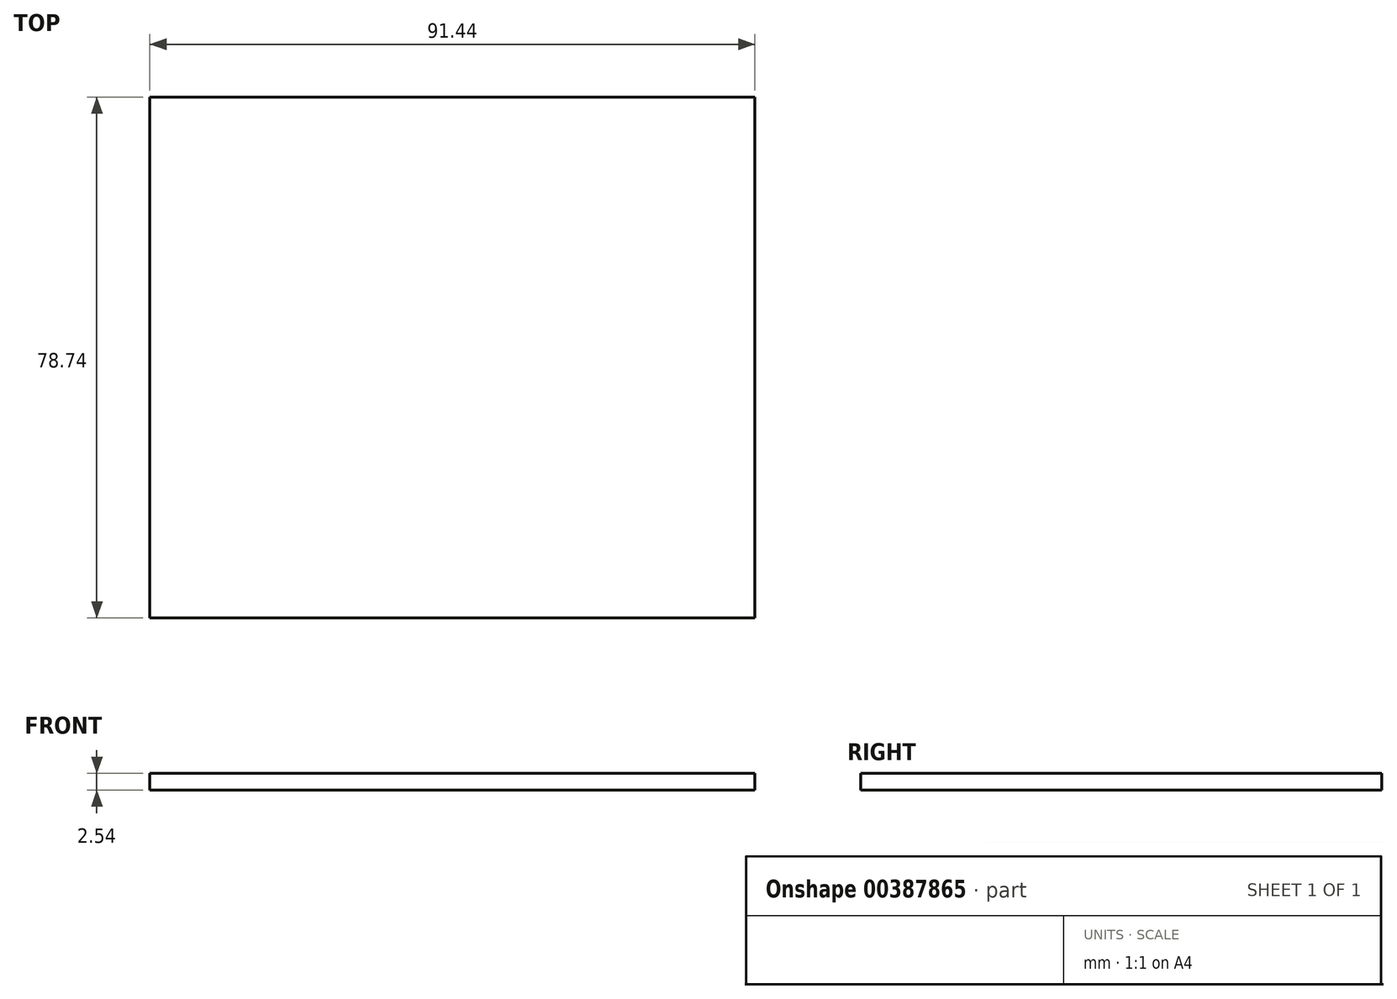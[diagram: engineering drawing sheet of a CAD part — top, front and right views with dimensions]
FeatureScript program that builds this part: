
annotation { "Feature Type Name" : "Feature", "Feature Type Description" : "" }
export const myFeature = defineFeature(function(context is Context, id is Id, definition is map)
    precondition{}
    {
        {
            var Q0;
            Q0=qCreatedBy(makeId("Top.planeOp"),FACE);
            var sketch = newSketch(context, id + "F0", { "sketchPlane" : qUnion([Q0])});
            skLineSegment(sketch, "E0.bottom", {"start": v(-45.06, 51.4) * mm, "end": v(46.38, 51.4) * mm});
            skLineSegment(sketch, "E0.top", {"start": v(-45.06, -27.35) * mm, "end": v(46.38, -27.35) * mm});
            skLineSegment(sketch, "E0.left", {"start": v(-45.06, 51.4) * mm, "end": v(-45.06, -27.35) * mm});
            skLineSegment(sketch, "E0.right", {"start": v(46.38, 51.4) * mm, "end": v(46.38, -27.35) * mm});
            skSolve(sketch);
        }
        {
            var Q0;
            Q0=makeQuery(id+"F0.imprint","IMPRINT",FACE,{"disambiguationData":[TD([[makeQuery(id+"F0.imprint","IMPRINT",EDGE,{"derivedFrom":sQuery(id+"F0.wireOp",EDGE,"E0.bottom")}),-1.0]])]});
            extrude(context, id + "F1", {"entities" : qUnion([Q0]), "depth" : 2.54 * mm});
        }
    });
